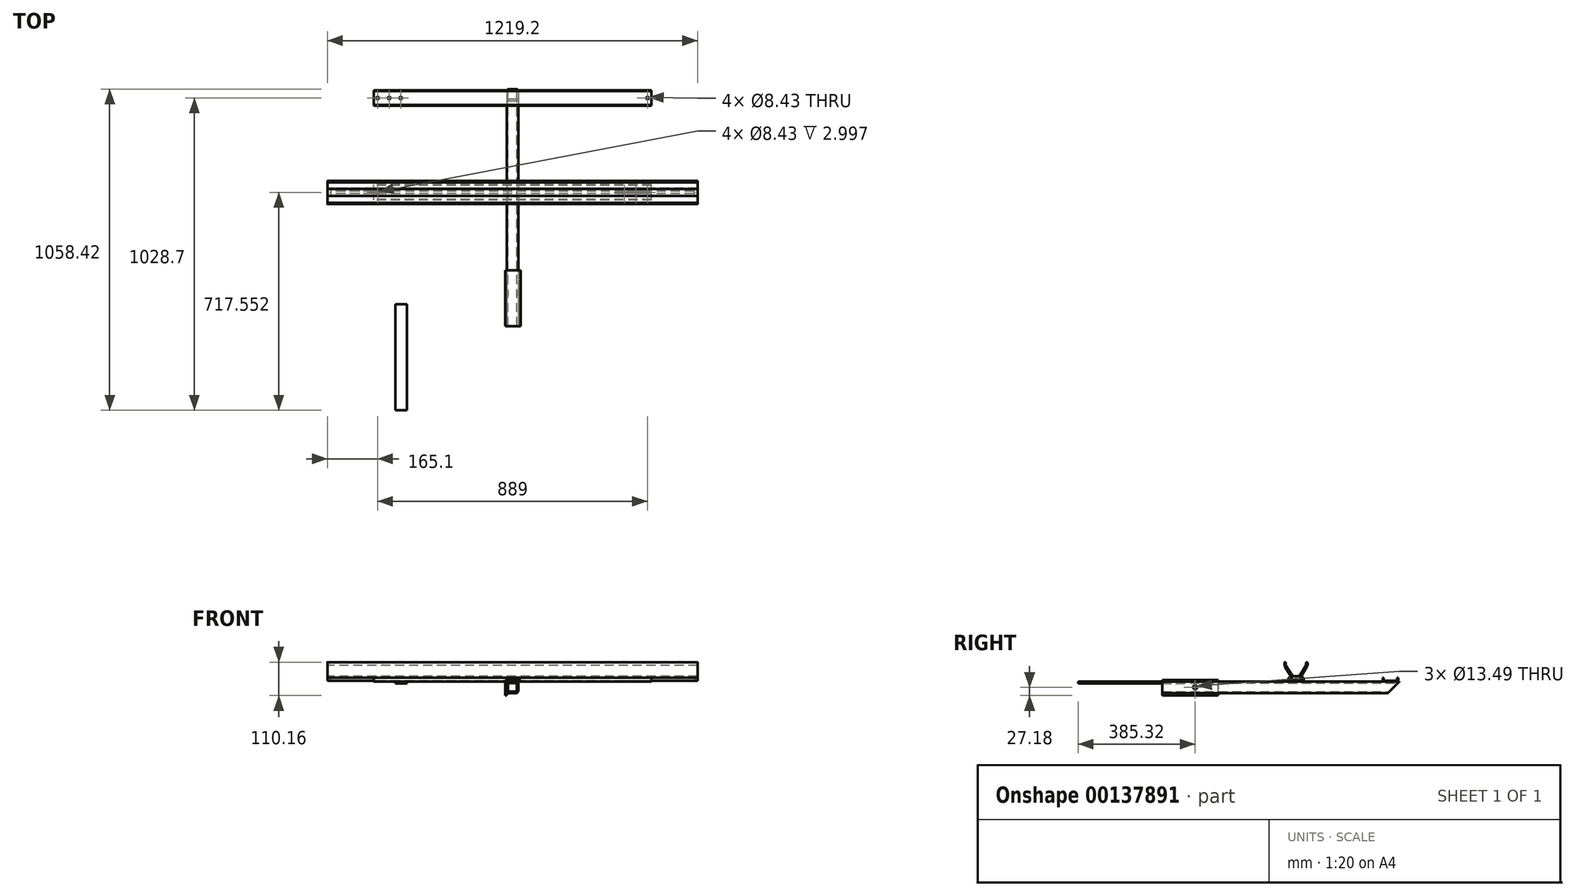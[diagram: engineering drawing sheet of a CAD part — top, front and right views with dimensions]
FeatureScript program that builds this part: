
annotation { "Feature Type Name" : "Feature", "Feature Type Description" : "" }
export const myFeature = defineFeature(function(context is Context, id is Id, definition is map)
    precondition{}
    {
        {
            var Q0;
            Q0=qCreatedBy(makeId("Front.planeOp"),FACE);
            var sketch = newSketch(context, id + "F0", { "sketchPlane" : qUnion([Q0])});
            skLineSegment(sketch, "E0.bottom", {"start": v(-19.05, 19.05) * mm, "end": v(19.05, 19.05) * mm});
            skLineSegment(sketch, "E0.top", {"start": v(-19.05, -19.05) * mm, "end": v(19.05, -19.05) * mm});
            skLineSegment(sketch, "E0.left", {"start": v(-19.05, 19.05) * mm, "end": v(-19.05, -19.05) * mm});
            skLineSegment(sketch, "E0.right", {"start": v(19.05, 19.05) * mm, "end": v(19.05, -19.05) * mm});
            skPoint(sketch, "E0.middle", {"position": v(0, 0) * mm});
            skSolve(sketch);
        }
        {
            var Q0;
            Q0 = qSketchRegion(id + "F0", true);
            extrude(context, id + "F1", {"entities" : qUnion([Q0]), "oppositeDirection" : true, "depth" : 781.05 * mm});
        }
        {
            var Q0;
            Q0=makeQuery(id+"F1.opExtrude","SWEPT_EDGE",EDGE,{"disambiguationData":[OSD([sQuery(id+"F0.wireOp",EDGE,"E0.top"),sQuery(id+"F0.wireOp",EDGE,"E0.left")])]});
            var Q1;
            Q1=makeQuery(id+"F1.opExtrude","SWEPT_EDGE",EDGE,{"disambiguationData":[OSD([sQuery(id+"F0.wireOp",EDGE,"E0.bottom"),sQuery(id+"F0.wireOp",EDGE,"E0.left")])]});
            var Q2;
            Q2=makeQuery(id+"F1.opExtrude","SWEPT_EDGE",EDGE,{"disambiguationData":[OSD([sQuery(id+"F0.wireOp",EDGE,"E0.top"),sQuery(id+"F0.wireOp",EDGE,"E0.right")])]});
            var Q3;
            Q3=makeQuery(id+"F1.opExtrude","SWEPT_EDGE",EDGE,{"disambiguationData":[OSD([sQuery(id+"F0.wireOp",EDGE,"E0.bottom"),sQuery(id+"F0.wireOp",EDGE,"E0.right")])]});
            fillet(context, id + "F2", {"entities" : qUnion([Q0, Q1, Q2, Q3]), "radius" : 7.62 * mm, "tangentPropagation" : true, "allowEdgeOverflow" : false});
        }
        {
            var Q0;
            Q0=makeQuery(id+"F1.opExtrude","CAP_FACE",FACE,{"disambiguationData":[OSD([sQuery(id+"F0.wireOp",EDGE,"E0.bottom"),sQuery(id+"F0.wireOp",EDGE,"E0.top"),sQuery(id+"F0.wireOp",EDGE,"E0.left"),sQuery(id+"F0.wireOp",EDGE,"E0.right")])],"isStart":false});
            var Q1;
            Q1=makeQuery(id+"F1.opExtrude","CAP_FACE",FACE,{"disambiguationData":[OSD([sQuery(id+"F0.wireOp",EDGE,"E0.bottom"),sQuery(id+"F0.wireOp",EDGE,"E0.top"),sQuery(id+"F0.wireOp",EDGE,"E0.left"),sQuery(id+"F0.wireOp",EDGE,"E0.right")])],"isStart":true});
            shell(context, id + "F3", {"entities" : qUnion([Q0, Q1]), "thickness" : 4.62 * mm});
        }
        {
            var Q0;
            Q0=qCreatedBy(makeId("Right.planeOp"),FACE);
            var sketch = newSketch(context, id + "F4", { "sketchPlane" : qUnion([Q0])});
            skLineSegment(sketch, "E1", {"start": v(781.05, -14.43) * mm, "end": v(781.05, -19.05) * mm});
            skLineSegment(sketch, "E2", {"start": v(781.05, 19.05) * mm, "end": v(781.05, 14.43) * mm});
            skLineSegment(sketch, "E3", {"start": v(0, -19.05) * mm, "end": v(781.05, -19.05) * mm});
            skLineSegment(sketch, "E4", {"start": v(781.05, 19.05) * mm, "end": v(742.95, -19.05) * mm});
            skLineSegment(sketch, "E5", {"start": v(742.95, -19.05) * mm, "end": v(781.05, -19.05) * mm});
            skLineSegment(sketch, "E6", {"start": v(781.05, 14.43) * mm, "end": v(781.05, -14.43) * mm});
            skSolve(sketch);
        }
        {
            var Q0;
            Q0 = qSketchRegion(id + "F4", true);
            extrude(context, id + "F5", {"entities" : qUnion([Q0]), "operationType" : NewBodyOperationType.REMOVE, "endBound" : BoundingType.SYMMETRIC, "oppositeDirection" : true, "depth" : 38.1 * mm});
        }
        {
            var Q0;
            Q0=qCreatedBy(makeId("Front.planeOp"),FACE);
            var sketch = newSketch(context, id + "F6", { "sketchPlane" : qUnion([Q0])});
            skLineSegment(sketch, "E7.bottom", {"start": v(-23.62, 23.62) * mm, "end": v(27.18, 23.62) * mm});
            skLineSegment(sketch, "E7.top", {"start": v(-23.62, -27.18) * mm, "end": v(-19.05, -27.18) * mm});
            skLineSegment(sketch, "E7.left", {"start": v(-23.62, 23.62) * mm, "end": v(-23.62, -27.18) * mm});
            skLineSegment(sketch, "E7.right", {"start": v(27.18, 23.62) * mm, "end": v(27.18, 19.05) * mm});
            skLineSegment(sketch, "E8", {"start": v(-19.05, -27.18) * mm, "end": v(-19.05, 19.05) * mm});
            skLineSegment(sketch, "E9", {"start": v(-19.05, 19.05) * mm, "end": v(27.18, 19.05) * mm});
            skSolve(sketch);
        }
        {
            var Q0;
            Q0 = qSketchRegion(id + "F6", true);
            extrude(context, id + "F7", {"entities" : qUnion([Q0]), "oppositeDirection" : true, "depth" : 184.15 * mm});
        }
        {
            var Q0;
            Q0=makeQuery(id+"F1.opExtrude","SWEPT_FACE",FACE,{"disambiguationData":[OSD([sQuery(id+"F0.wireOp",EDGE,"E0.right")])]});
            var sketch = newSketch(context, id + "F8", { "sketchPlane" : qUnion([Q0])});
            skPoint(sketch, "E10", {"position": v(107.95, 0) * mm});
            skSolve(sketch);
        }
        {
            var Q0;
            Q0=sQuery(id+"F8.wireOp",VERTEX,"E10");
            var Q1;
            Q1=makeQuery(id+"F1.opExtrude","SWEPT_BODY",BODY,{"disambiguationData":[OSD([sQuery(id+"F0.wireOp",EDGE,"E0.bottom"),sQuery(id+"F0.wireOp",EDGE,"E0.top"),sQuery(id+"F0.wireOp",EDGE,"E0.left"),sQuery(id+"F0.wireOp",EDGE,"E0.right")])]});
            var Q2;
            Q2=makeQuery(id+"F7.opExtrude","SWEPT_BODY",BODY,{"disambiguationData":[OSD([sQuery(id+"F6.wireOp",EDGE,"E7.bottom"),sQuery(id+"F6.wireOp",EDGE,"E7.top"),sQuery(id+"F6.wireOp",EDGE,"E7.left"),sQuery(id+"F6.wireOp",EDGE,"E7.right"),sQuery(id+"F6.wireOp",EDGE,"E8"),sQuery(id+"F6.wireOp",EDGE,"E9")])]});
            hole(context, id + "F9", {"style" : HoleStyle.SIMPLE, "endStyle" : HoleEndStyle.THROUGH, "standardTappedOrClearance" : lookupTablePath({ "standard" : "ANSI", "fit" : "Normal (ASME)", "size" : "1/2", "type" : "Clearance" }), "standardBlindInLast" : lookupTablePath({ "fit" : "Free", "standard" : "ANSI", "size" : "1/2", "type" : "Clearance" }), "holeDiameter" : 13.5 * mm, "locations" : qUnion([Q0]), "scope" : qUnion([Q1, Q2]), "isTappedThrough" : true});
        }
        {
            var Q0;
            Q0=qCreatedBy(makeId("Right.planeOp"),FACE);
            var sketch = newSketch(context, id + "F10", { "sketchPlane" : qUnion([Q0])});
            skLineSegment(sketch, "E11.top", {"start": v(725.93, 19.05) * mm, "end": v(776.73, 19.05) * mm});
            skLineSegment(sketch, "E11.left", {"start": v(725.93, 31.75) * mm, "end": v(725.93, 19.05) * mm});
            skLineSegment(sketch, "E11.right", {"start": v(776.73, 31.75) * mm, "end": v(776.73, 19.05) * mm});
            skLineSegment(sketch, "E12", {"start": v(725.93, 31.75) * mm, "end": v(776.73, 31.75) * mm});
            skLineSegment(sketch, "E13", {"start": v(751.33, 19.05) * mm, "end": v(751.33, 31.75) * mm, "construction": true});
            skSolve(sketch);
        }
        {
            var Q0;
            Q0 = qSketchRegion(id + "F10", true);
            extrude(context, id + "F11", {"entities" : qUnion([Q0]), "endBound" : BoundingType.SYMMETRIC, "depth" : 914.4 * mm, "hasSecondDirection" : true, "secondDirectionOppositeDirection" : true, "secondDirectionDepth" : 25.4 * mm});
        }
        {
            var Q0;
            Q0=makeQuery(id+"F11.opExtrude","SWEPT_EDGE",EDGE,{"disambiguationData":[OSD([sQuery(id+"F10.wireOp",EDGE,"E11.top"),sQuery(id+"F10.wireOp",EDGE,"E11.left")])]});
            var Q1;
            Q1=makeQuery(id+"F11.opExtrude","SWEPT_EDGE",EDGE,{"disambiguationData":[OSD([sQuery(id+"F10.wireOp",EDGE,"E11.top"),sQuery(id+"F10.wireOp",EDGE,"E11.right")])]});
            fillet(context, id + "F12", {"entities" : qUnion([Q0, Q1]), "radius" : 5.08 * mm, "tangentPropagation" : true, "allowEdgeOverflow" : false});
        }
        {
            var Q0;
            Q0=makeQuery(id+"F11.opExtrude","SWEPT_FACE",FACE,{"disambiguationData":[OSD([sQuery(id+"F10.wireOp",EDGE,"E12")])]});
            var Q1;
            Q1=makeQuery(id+"F11.opExtrude","CAP_FACE",FACE,{"disambiguationData":[OSD([sQuery(id+"F10.wireOp",EDGE,"E11.top"),sQuery(id+"F10.wireOp",EDGE,"E11.left"),sQuery(id+"F10.wireOp",EDGE,"E11.right"),sQuery(id+"F10.wireOp",EDGE,"E12")])],"isStart":false});
            var Q2;
            Q2=makeQuery(id+"F11.opExtrude","CAP_FACE",FACE,{"disambiguationData":[OSD([sQuery(id+"F10.wireOp",EDGE,"E11.top"),sQuery(id+"F10.wireOp",EDGE,"E11.left"),sQuery(id+"F10.wireOp",EDGE,"E11.right"),sQuery(id+"F10.wireOp",EDGE,"E12")])],"isStart":true});
            shell(context, id + "F13", {"entities" : qUnion([Q0, Q1, Q2]), "thickness" : 3 * mm});
        }
        {
            var Q0;
            Q0=makeQuery(id+"F13.opShell","OFFSET_FACE",FACE,{"disambiguationData":[OSD([sQuery(id+"F10.wireOp",EDGE,"E11.top")])]});
            var sketch = newSketch(context, id + "F14", { "sketchPlane" : qUnion([Q0])});
            skPoint(sketch, "E14", {"position": v(406.4, 751.33) * mm});
            skPoint(sketch, "E14.positionSnap0", {"position": v(457.2, 751.33) * mm});
            skPoint(sketch, "E15", {"position": v(368.3, 751.33) * mm});
            skPoint(sketch, "E16", {"position": v(444.5, 751.33) * mm});
            skPoint(sketch, "E17", {"position": v(-444.5, 751.33) * mm});
            skPoint(sketch, "E17.positionSnap0", {"position": v(-457.2, 751.33) * mm});
            skSolve(sketch);
        }
        {
            var Q0;
            Q0=sQuery(id+"F14.wireOp",VERTEX,"E14");
            var Q1;
            Q1=sQuery(id+"F14.wireOp",VERTEX,"E15");
            var Q2;
            Q2=sQuery(id+"F14.wireOp",VERTEX,"E16");
            var Q3;
            Q3=sQuery(id+"F14.wireOp",VERTEX,"E17");
            var Q4;
            Q4=makeQuery(id+"F11.opExtrude","SWEPT_BODY",BODY,{"disambiguationData":[OSD([sQuery(id+"F10.wireOp",EDGE,"E11.top"),sQuery(id+"F10.wireOp",EDGE,"E11.left"),sQuery(id+"F10.wireOp",EDGE,"E11.right"),sQuery(id+"F10.wireOp",EDGE,"E12")])]});
            hole(context, id + "F15", {"style" : HoleStyle.SIMPLE, "endStyle" : HoleEndStyle.THROUGH, "standardTappedOrClearance" : lookupTablePath({ "standard" : "ANSI", "fit" : "Normal (ASME)", "size" : "5/16", "type" : "Clearance" }), "standardBlindInLast" : lookupTablePath({ "fit" : "Free", "standard" : "ANSI", "size" : "5/16", "type" : "Clearance" }), "holeDiameter" : 8.43 * mm, "locations" : qUnion([Q0, Q1, Q2, Q3]), "scope" : qUnion([Q4]), "isTappedThrough" : true});
        }
        {
            var Q0;
            Q0=makeQuery(id+"F11.opExtrude","SWEPT_BODY",BODY,{"disambiguationData":[OSD([sQuery(id+"F10.wireOp",EDGE,"E11.top"),sQuery(id+"F10.wireOp",EDGE,"E11.left"),sQuery(id+"F10.wireOp",EDGE,"E11.right"),sQuery(id+"F10.wireOp",EDGE,"E12")])]});
            transform(context, id + "F16", {"entities" : qUnion([Q0]), "transformType" : TransformType.TRANSLATION_3D, "dx" : 0 * mm, "dy" : -311.15 * mm, "dz" : 0 * mm, "makeCopy" : true});
        }
        {
            var Q0;
            Q0=makeQuery(id+"F11.opExtrude","SWEPT_BODY",BODY,{"disambiguationData":[OSD([sQuery(id+"F10.wireOp",EDGE,"E11.top"),sQuery(id+"F10.wireOp",EDGE,"E11.left"),sQuery(id+"F10.wireOp",EDGE,"E11.right"),sQuery(id+"F10.wireOp",EDGE,"E12")])]});
            var Q1;
            Q1=sQuery(id+"F10.wireOp",EDGE,"E13");
            transform(context, id + "F17", {"entities" : qUnion([Q0]), "transformType" : TransformType.ROTATION, "transformAxis" : qUnion([Q1]), "angle" : 180 * degree, "makeCopy" : false});
        }
        {
            var Q0;
            Q0=makeQuery(id+"F11.opExtrude","SWEPT_FACE",FACE,{"disambiguationData":[OSD([sQuery(id+"F10.wireOp",EDGE,"E11.top")])]});
            var sketch = newSketch(context, id + "F18", { "sketchPlane" : qUnion([Q0])});
            skLineSegment(sketch, "E18.top", {"start": v(-347.98, 277.37) * mm, "end": v(-386.08, 277.37) * mm});
            skLineSegment(sketch, "E18.left", {"start": v(-386.08, 277.37) * mm, "end": v(-386.08, -71.88) * mm});
            skLineSegment(sketch, "E18.right", {"start": v(-347.98, 277.37) * mm, "end": v(-347.98, -71.88) * mm});
            skLineSegment(sketch, "E19", {"start": v(-347.98, -71.88) * mm, "end": v(-386.08, -71.88) * mm});
            skSolve(sketch);
        }
        {
            var Q0;
            Q0 = qSketchRegion(id + "F18", true);
            extrude(context, id + "F19", {"entities" : qUnion([Q0]), "depth" : 6.35 * mm});
        }
        {
            var Q0;
            Q0=qCreatedBy(makeId("Right.planeOp"),FACE);
            var sketch = newSketch(context, id + "F20", { "sketchPlane" : qUnion([Q0])});
            skLineSegment(sketch, "E20.bottom", {"start": v(425.9, 22.05) * mm, "end": v(454.47, 22.05) * mm});
            skLineSegment(sketch, "E20.top", {"start": v(425.9, 32.2) * mm, "end": v(454.47, 32.2) * mm});
            skLineSegment(sketch, "E20.left", {"start": v(425.9, 22.05) * mm, "end": v(425.9, 32.2) * mm});
            skLineSegment(sketch, "E20.right", {"start": v(454.47, 22.05) * mm, "end": v(454.47, 32.2) * mm});
            skLineSegment(sketch, "E21", {"start": v(440.18, 22.05) * mm, "end": v(440.18, 32.2) * mm, "construction": true});
            skLineSegment(sketch, "E22", {"start": v(425.9, 32.2) * mm, "end": v(402.08, 71.55) * mm});
            skLineSegment(sketch, "E23", {"start": v(402.08, 71.55) * mm, "end": v(402.08, 83) * mm});
            skLineSegment(sketch, "E24.MirrorCS", {"start": v(478.28, 71.55) * mm, "end": v(478.28, 83) * mm});
            skLineSegment(sketch, "E25.MirrorCS", {"start": v(454.47, 32.2) * mm, "end": v(478.28, 71.55) * mm});
            skLineSegment(sketch, "E26", {"start": v(402.08, 83) * mm, "end": v(478.28, 83) * mm});
            skLineSegment(sketch, "E27", {"start": v(460.5, 22.05) * mm, "end": v(419.86, 22.05) * mm, "construction": true});
            skSolve(sketch);
        }
        {
            var Q0;
            Q0=makeQuery(id+"F20.imprint","IMPRINT",FACE,{"disambiguationData":[TD([[makeQuery(id+"F20.imprint","IMPRINT",EDGE,{"derivedFrom":sQuery(id+"F20.wireOp",EDGE,"E20.top")}),1.0]])]});
            extrude(context, id + "F21", {"entities" : qUnion([Q0]), "endBound" : BoundingType.SYMMETRIC, "depth" : 1219.2 * mm});
        }
        {
            var Q0;
            Q0=makeQuery(id+"F21.opExtrude","CAP_FACE",FACE,{"disambiguationData":[OSD([sQuery(id+"F20.wireOp",EDGE,"E20.top"),sQuery(id+"F20.wireOp",EDGE,"E22"),sQuery(id+"F20.wireOp",EDGE,"E23"),sQuery(id+"F20.wireOp",EDGE,"E24.MirrorCS"),sQuery(id+"F20.wireOp",EDGE,"E25.MirrorCS"),sQuery(id+"F20.wireOp",EDGE,"E26")])],"isStart":false});
            var Q1;
            Q1=makeQuery(id+"F21.opExtrude","SWEPT_FACE",FACE,{"disambiguationData":[OSD([sQuery(id+"F20.wireOp",EDGE,"E26")])]});
            var Q2;
            Q2=makeQuery(id+"F21.opExtrude","CAP_FACE",FACE,{"disambiguationData":[OSD([sQuery(id+"F20.wireOp",EDGE,"E20.top"),sQuery(id+"F20.wireOp",EDGE,"E22"),sQuery(id+"F20.wireOp",EDGE,"E23"),sQuery(id+"F20.wireOp",EDGE,"E24.MirrorCS"),sQuery(id+"F20.wireOp",EDGE,"E25.MirrorCS"),sQuery(id+"F20.wireOp",EDGE,"E26")])],"isStart":true});
            shell(context, id + "F22", {"entities" : qUnion([Q0, Q1, Q2]), "thickness" : 4.57 * mm});
        }
        {
            var Q0;
            Q0=makeQuery(id+"F20.imprint","IMPRINT",FACE,{"disambiguationData":[TD([[makeQuery(id+"F20.imprint","IMPRINT",EDGE,{"derivedFrom":sQuery(id+"F20.wireOp",EDGE,"E20.bottom")}),1.0]])]});
            extrude(context, id + "F23", {"entities" : qUnion([Q0]), "operationType" : NewBodyOperationType.ADD, "endBound" : BoundingType.SYMMETRIC, "depth" : 1219.2 * mm});
        }
        {
            var Q0;
            Q0=makeQuery(id+"F21.opExtrude","SWEPT_EDGE",EDGE,{"disambiguationData":[OSD([sQuery(id+"F20.wireOp",EDGE,"E24.MirrorCS"),sQuery(id+"F20.wireOp",EDGE,"E26")])]});
            var Q1;
            Q1=makeQuery(id+"F22.opShell","OFFSET_EDGE",EDGE,{"disambiguationData":[OSD([sQuery(id+"F20.wireOp",EDGE,"E24.MirrorCS"),sQuery(id+"F20.wireOp",EDGE,"E26")])]});
            var Q2;
            Q2=makeQuery(id+"F21.opExtrude","SWEPT_EDGE",EDGE,{"disambiguationData":[OSD([sQuery(id+"F20.wireOp",EDGE,"E23"),sQuery(id+"F20.wireOp",EDGE,"E26")])]});
            var Q3;
            Q3=makeQuery(id+"F22.opShell","OFFSET_EDGE",EDGE,{"disambiguationData":[OSD([sQuery(id+"F20.wireOp",EDGE,"E23"),sQuery(id+"F20.wireOp",EDGE,"E26")])]});
            fillet(context, id + "F24", {"entities" : qUnion([Q0, Q1, Q2, Q3]), "radius" : 2.54 * mm, "tangentPropagation" : true, "allowEdgeOverflow" : false});
        }
        {
            var Q0;
            Q0=makeQuery(id+"F21.opExtrude","SWEPT_EDGE",EDGE,{"disambiguationData":[OSD([sQuery(id+"F20.wireOp",EDGE,"E24.MirrorCS"),sQuery(id+"F20.wireOp",EDGE,"E25.MirrorCS")])]});
            var Q1;
            Q1=makeQuery(id+"F21.opExtrude","SWEPT_EDGE",EDGE,{"disambiguationData":[OSD([sQuery(id+"F20.wireOp",EDGE,"E22"),sQuery(id+"F20.wireOp",EDGE,"E23")])]});
            fillet(context, id + "F25", {"entities" : qUnion([Q0, Q1]), "radius" : 12.7 * mm, "tangentPropagation" : true, "allowEdgeOverflow" : false});
        }
        {
            var Q0;
            Q0=makeQuery(id+"F23.opExtrude","SWEPT_FACE",FACE,{"disambiguationData":[OSD([sQuery(id+"F20.wireOp",EDGE,"E20.bottom")])]});
            var sketch = newSketch(context, id + "F26", { "sketchPlane" : qUnion([Q0])});
            skLineSegment(sketch, "E28", {"start": v(596.9, -440.18) * mm, "end": v(-596.9, -440.18) * mm, "construction": true});
            skPoint(sketch, "E28.startSnap0", {"position": v(609.6, -440.18) * mm});
            skArc(sketch, "E29.0.startCap", {"start": v(596.9, -436.24) * mm, "mid": v(600.84, -440.18) * mm, "end": v(596.9, -444.12) * mm});
            skArc(sketch, "E29.0.endCap", {"start": v(-596.9, -444.12) * mm, "mid": v(-600.84, -440.18) * mm, "end": v(-596.9, -436.24) * mm});
            skLineSegment(sketch, "E29.0.left", {"start": v(596.9, -444.12) * mm, "end": v(-596.9, -444.12) * mm});
            skLineSegment(sketch, "E29.0.right", {"start": v(596.9, -436.24) * mm, "end": v(-596.9, -436.24) * mm});
            skSolve(sketch);
        }
        {
            var Q0;
            Q0 = qSketchRegion(id + "F26", true);
            extrude(context, id + "F27", {"entities" : qUnion([Q0]), "operationType" : NewBodyOperationType.REMOVE, "oppositeDirection" : true, "depth" : 7.62 * mm});
        }
    });
